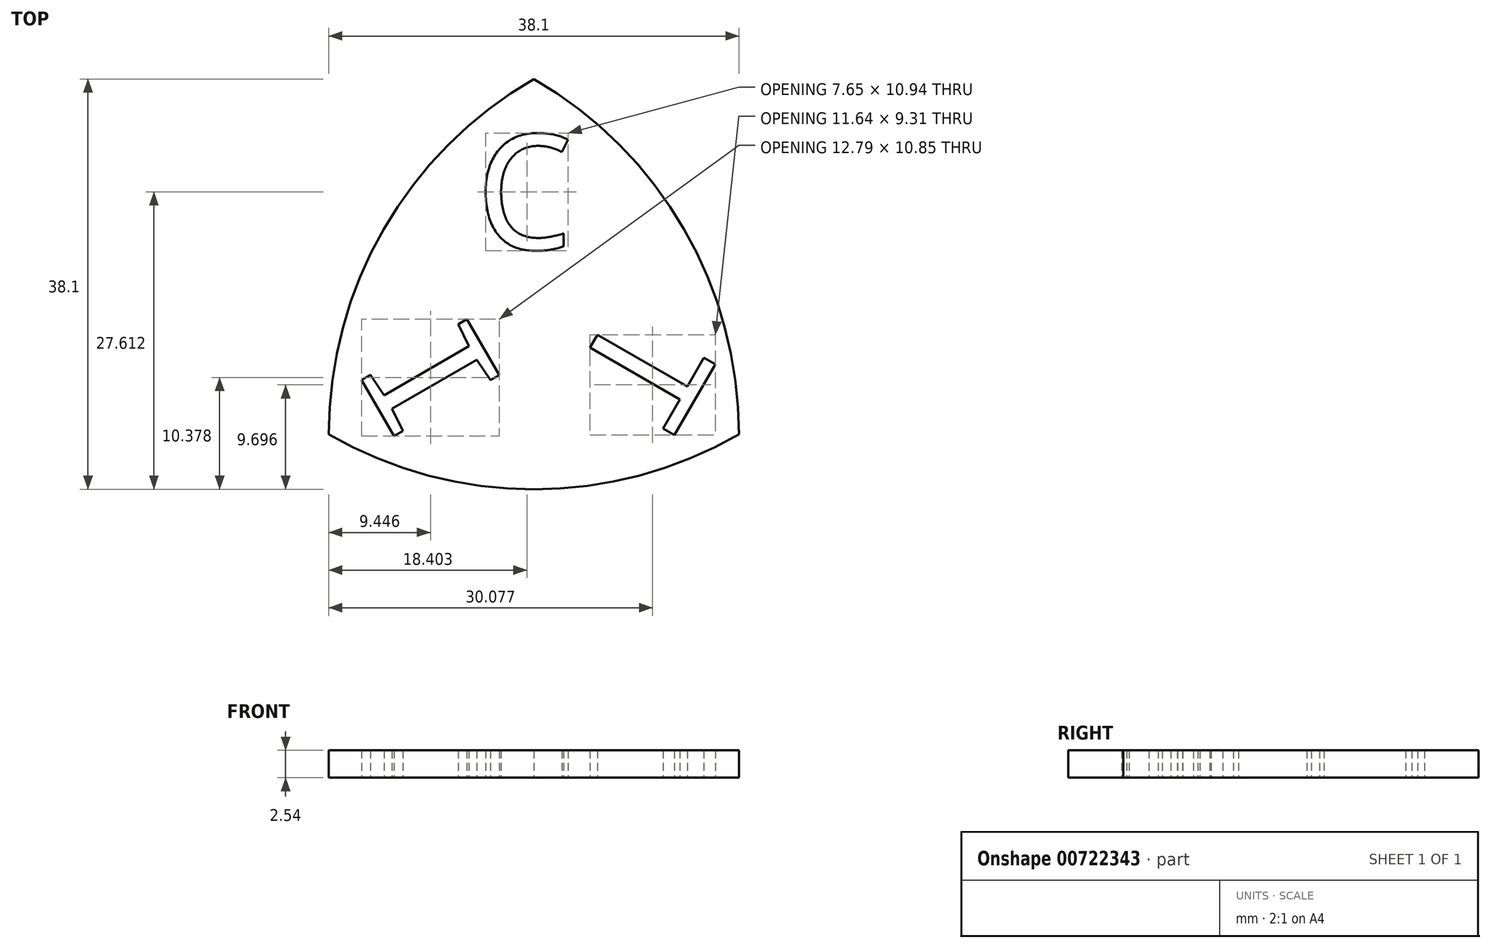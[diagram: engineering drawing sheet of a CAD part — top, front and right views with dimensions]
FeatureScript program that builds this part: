
annotation { "Feature Type Name" : "Feature", "Feature Type Description" : "" }
export const myFeature = defineFeature(function(context is Context, id is Id, definition is map)
    precondition{}
    {
        {
            var Q0;
            Q0=qCreatedBy(makeId("Top.planeOp"),FACE);
            var sketch = newSketch(context, id + "F0", { "sketchPlane" : qUnion([Q0])});
            skCircle(sketch, "E0", {"center": v(0, 0) * mm, "radius": 38.1 * mm});
            skSolve(sketch);
        }
        {
            var Q0;
            Q0=qCreatedBy(makeId("Top.planeOp"),FACE);
            var sketch = newSketch(context, id + "F1", { "sketchPlane" : qUnion([Q0])});
            skCircle(sketch, "E1", {"center": v(-38.1, 0) * mm, "radius": 38.1 * mm});
            skSolve(sketch);
        }
        {
            var Q0;
            Q0=qCreatedBy(makeId("Top.planeOp"),FACE);
            var sketch = newSketch(context, id + "F2", { "sketchPlane" : qUnion([Q0])});
            skCircle(sketch, "E2", {"center": v(-19.05, 33) * mm, "radius": 38.1 * mm});
            skSolve(sketch);
        }
        {
            var Q0;
            Q0 = qSketchRegion(id + "F0", true);
            var Q1;
            Q1 = qSketchRegion(id + "F1", true);
            var Q2;
            Q2 = qSketchRegion(id + "F2", true);
            extrude(context, id + "F3", {"entities" : qUnion([Q0, Q1, Q2]), "depth" : 2.54 * mm, "offsetDistance" : 25.4 * mm});
        }
        {
            var Q0;
            Q0=makeQuery(id+"F3.opExtrude","SWEPT_BODY",BODY,{"disambiguationData":[OSD([sQuery(id+"F0.wireOp",EDGE,"E0")])]});
            var Q1;
            Q1=makeQuery(id+"F3.opExtrude","SWEPT_BODY",BODY,{"disambiguationData":[OSD([sQuery(id+"F1.wireOp",EDGE,"E1")])]});
            var Q2;
            Q2=makeQuery(id+"F3.opExtrude","SWEPT_BODY",BODY,{"disambiguationData":[OSD([sQuery(id+"F2.wireOp",EDGE,"E2")])]});
            booleanBodies(context, id + "F4", {"operationType" : BooleanOperationType.INTERSECTION, "tools" : qUnion([Q0, Q1, Q2])});
        }
        {
            var Q0;
            Q0=qCreatedBy(makeId("Top.planeOp"),FACE);
            var sketch = newSketch(context, id + "F5", { "sketchPlane" : qUnion([Q0])});
            skText(sketch, "E3", { "text": "I\n", "fontName": "DroidSansMono.ttf"});
            skText(sketch, "E4", { "text": "T", "fontName": "DroidSansMono.ttf"});
            skText(sketch, "E5", { "text": "C", "fontName": "DroidSansMono.ttf"});
            const initialGuessF5  = {"E3": [-0.02139, 0.004, -0.5, 0.86603, 0.0114], "E4": [-0.01122, 0.01259, -0.5, -0.86603, 0.01094], "E5": [-0.02446, 0.01719, 1, 0, 0.01073]};
            skSetInitialGuess(sketch, initialGuessF5);
            skSolve(sketch);
        }
        {
            var Q0;
            Q0 = qSketchRegion(id + "F5", true);
            extrude(context, id + "F6", {"entities" : qUnion([Q0]), "depth" : 2.54 * mm, "offsetDistance" : 25.4 * mm});
        }
        {
            var Q0;
            Q0=makeQuery(id+"F6.opExtrude","SWEPT_BODY",BODY,{"disambiguationData":[OSD([sQuery(id+"F5.wireOp",EDGE,"E3.sketch_text.stroke-0"),sQuery(id+"F5.wireOp",EDGE,"E3.sketch_text.stroke-1"),sQuery(id+"F5.wireOp",EDGE,"E3.sketch_text.stroke-2"),sQuery(id+"F5.wireOp",EDGE,"E3.sketch_text.stroke-3"),sQuery(id+"F5.wireOp",EDGE,"E3.sketch_text.stroke-4"),sQuery(id+"F5.wireOp",EDGE,"E3.sketch_text.stroke-5"),sQuery(id+"F5.wireOp",EDGE,"E3.sketch_text.stroke-6"),sQuery(id+"F5.wireOp",EDGE,"E3.sketch_text.stroke-7"),sQuery(id+"F5.wireOp",EDGE,"E3.sketch_text.stroke-8"),sQuery(id+"F5.wireOp",EDGE,"E3.sketch_text.stroke-9"),sQuery(id+"F5.wireOp",EDGE,"E3.sketch_text.stroke-10"),sQuery(id+"F5.wireOp",EDGE,"E3.sketch_text.stroke-11")])]});
            var Q1;
            Q1=makeQuery(id+"F6.opExtrude","SWEPT_BODY",BODY,{"disambiguationData":[OSD([sQuery(id+"F5.wireOp",EDGE,"E4.sketch_text.stroke-0"),sQuery(id+"F5.wireOp",EDGE,"E4.sketch_text.stroke-1"),sQuery(id+"F5.wireOp",EDGE,"E4.sketch_text.stroke-2"),sQuery(id+"F5.wireOp",EDGE,"E4.sketch_text.stroke-3"),sQuery(id+"F5.wireOp",EDGE,"E4.sketch_text.stroke-4"),sQuery(id+"F5.wireOp",EDGE,"E4.sketch_text.stroke-5"),sQuery(id+"F5.wireOp",EDGE,"E4.sketch_text.stroke-6"),sQuery(id+"F5.wireOp",EDGE,"E4.sketch_text.stroke-7")])]});
            var Q2;
            Q2=makeQuery(id+"F6.opExtrude","SWEPT_BODY",BODY,{"disambiguationData":[OSD([sQuery(id+"F5.wireOp",EDGE,"E5.sketch_text.stroke-0"),sQuery(id+"F5.wireOp",EDGE,"E5.sketch_text.stroke-1"),sQuery(id+"F5.wireOp",EDGE,"E5.sketch_text.stroke-2"),sQuery(id+"F5.wireOp",EDGE,"E5.sketch_text.stroke-3"),sQuery(id+"F5.wireOp",EDGE,"E5.sketch_text.stroke-4"),sQuery(id+"F5.wireOp",EDGE,"E5.sketch_text.stroke-5"),sQuery(id+"F5.wireOp",EDGE,"E5.sketch_text.stroke-6"),sQuery(id+"F5.wireOp",EDGE,"E5.sketch_text.stroke-7"),sQuery(id+"F5.wireOp",EDGE,"E5.sketch_text.stroke-8"),sQuery(id+"F5.wireOp",EDGE,"E5.sketch_text.stroke-9"),sQuery(id+"F5.wireOp",EDGE,"E5.sketch_text.stroke-10"),sQuery(id+"F5.wireOp",EDGE,"E5.sketch_text.stroke-11"),sQuery(id+"F5.wireOp",EDGE,"E5.sketch_text.stroke-12"),sQuery(id+"F5.wireOp",EDGE,"E5.sketch_text.stroke-13")])]});
            var Q3;
            Q3=makeQuery(id+"F4.opBoolean","INTERSECT",BODY,{"derivedFrom":[makeQuery(id+"F3.opExtrude","SWEPT_BODY",BODY,{"disambiguationData":[OSD([sQuery(id+"F0.wireOp",EDGE,"E0")])]}),makeQuery(id+"F3.opExtrude","SWEPT_BODY",BODY,{"disambiguationData":[OSD([sQuery(id+"F1.wireOp",EDGE,"E1")])]}),makeQuery(id+"F3.opExtrude","SWEPT_BODY",BODY,{"disambiguationData":[OSD([sQuery(id+"F2.wireOp",EDGE,"E2")])]})]});
            booleanBodies(context, id + "F7", {"operationType" : BooleanOperationType.SUBTRACTION, "tools" : qUnion([Q0, Q1, Q2]), "targets" : qUnion([Q3])});
        }
    });
